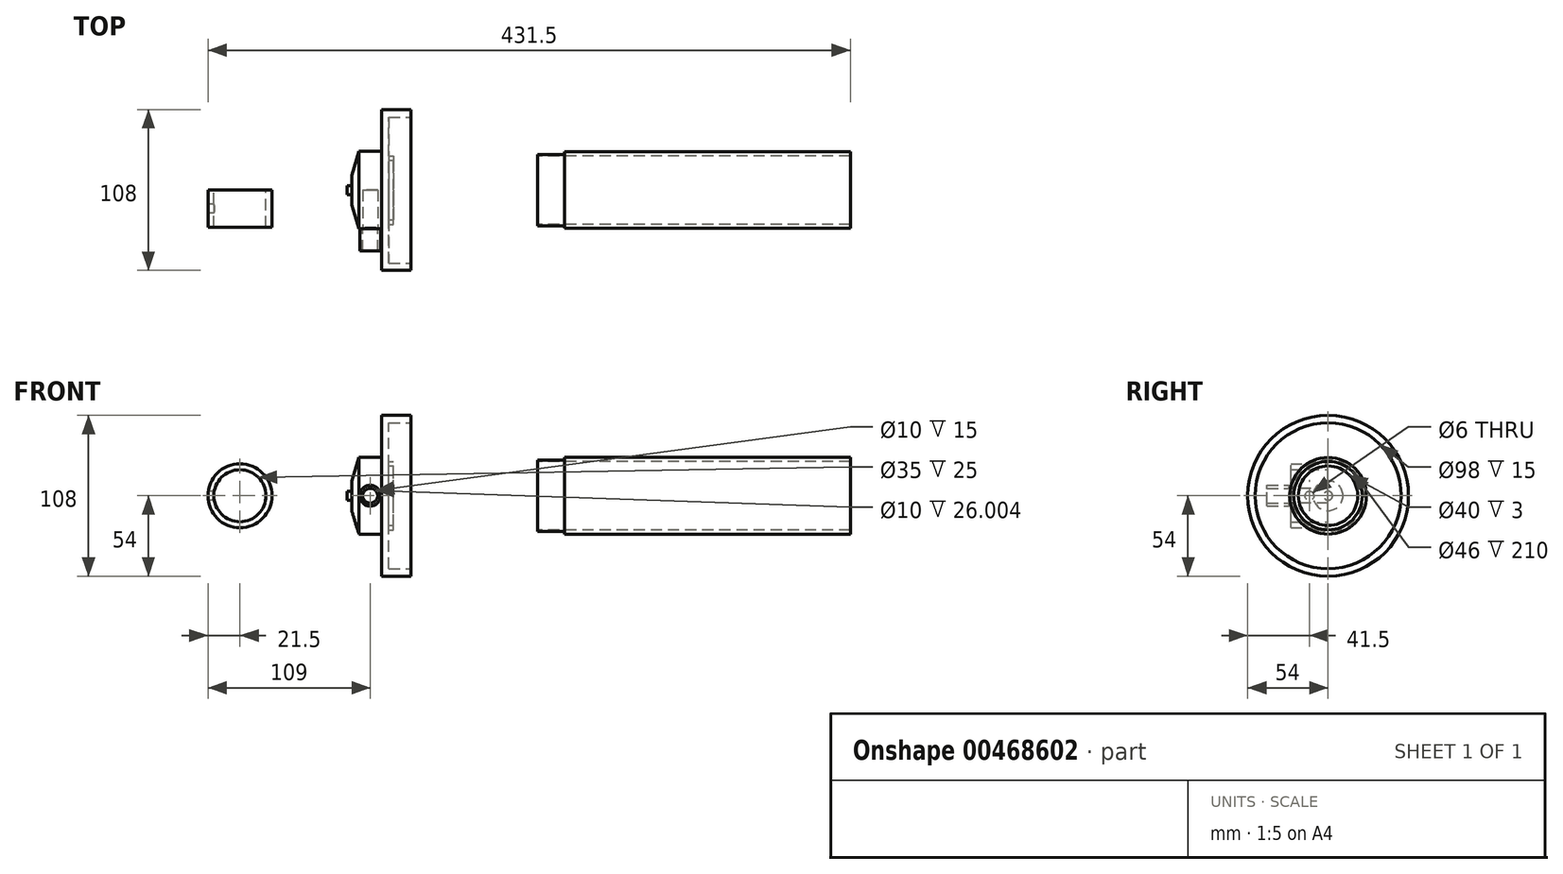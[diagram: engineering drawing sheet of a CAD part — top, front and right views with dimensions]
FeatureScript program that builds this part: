
annotation { "Feature Type Name" : "Feature", "Feature Type Description" : "" }
export const myFeature = defineFeature(function(context is Context, id is Id, definition is map)
    precondition{}
    {
        {
            var Q0;
            Q0=qCreatedBy(makeId("Front.planeOp"),FACE);
            var sketch = newSketch(context, id + "F0", { "sketchPlane" : qUnion([Q0])});
            skLineSegment(sketch, "E0", {"start": v(0, 0) * mm, "end": v(0, 25.75) * mm});
            skLineSegment(sketch, "E1", {"start": v(0, 25.75) * mm, "end": v(210, 25.75) * mm});
            skLineSegment(sketch, "E2", {"start": v(210, 25.75) * mm, "end": v(210, 23) * mm});
            skLineSegment(sketch, "E3", {"start": v(210, 23) * mm, "end": v(0, 23) * mm});
            skLineSegment(sketch, "E4", {"start": v(0, 0) * mm, "end": v(100, 0) * mm, "construction": true});
            skSolve(sketch);
        }
        {
            var Q0;
            Q0=qSketchRegion(id+"F0",true);
            var Q1;
            Q1=sQuery(id+"F0.wireOp",EDGE,"E4");
            revolve(context, id + "F1", {"entities" : qUnion([Q0]), "axis" : qUnion([Q1]), "revolveType" : RevolveType.FULL});
        }
        {
            var Q0;
            Q0=makeQuery(id+"F1.opRevolve","SWEPT_FACE",FACE,{"disambiguationData":[OSD([sQuery(id+"F0.wireOp",EDGE,"E0")])]});
            var sketch = newSketch(context, id + "F2", { "sketchPlane" : qUnion([Q0])});
            skCircle(sketch, "E5", {"center": v(0, 0) * mm, "radius": 24 * mm});
            skCircle(sketch, "E6.0", {"center": v(0, 0) * mm, "radius": 25.75 * mm});
            skSolve(sketch);
        }
        {
            var Q0;
            Q0=qSketchRegion(id+"F2",true);
            extrude(context, id + "F3", {"entities" : qUnion([Q0]), "operationType" : NewBodyOperationType.REMOVE, "oppositeDirection" : true, "depth" : 18 * mm});
        }
        {
            var Q0;
            Q0=qCreatedBy(makeId("Front.planeOp"),FACE);
            var sketch = newSketch(context, id + "F4", { "sketchPlane" : qUnion([Q0])});
            skLineSegment(sketch, "E7", {"start": v(0, 0) * mm, "end": v(-100, 0) * mm, "construction": true});
            skLineSegment(sketch, "E8", {"start": v(-100, 0) * mm, "end": v(-100, 26) * mm});
            skLineSegment(sketch, "E9", {"start": v(-100, 26) * mm, "end": v(-120, 26) * mm});
            skPoint(sketch, "E10", {"position": v(-100, 23) * mm});
            skLineSegment(sketch, "E11", {"start": v(-100, 23) * mm, "end": v(-97, 23) * mm});
            skLineSegment(sketch, "E12", {"start": v(-97, 23) * mm, "end": v(-97, 20) * mm});
            skLineSegment(sketch, "E13", {"start": v(-97, 20) * mm, "end": v(-100, 20) * mm});
            skLineSegment(sketch, "E14", {"start": v(-100, 0) * mm, "end": v(-125, 0) * mm});
            skLineSegment(sketch, "E15", {"start": v(-125, 0) * mm, "end": v(-125, 10) * mm});
            skLineSegment(sketch, "E16", {"start": v(-125, 10) * mm, "end": v(-120, 26) * mm});
            skLineSegment(sketch, "E17", {"start": v(-125, 0) * mm, "end": v(-128, 0) * mm});
            skLineSegment(sketch, "E18", {"start": v(-128, 0) * mm, "end": v(-128, 3) * mm});
            skLineSegment(sketch, "E19", {"start": v(-128, 3) * mm, "end": v(-125, 3) * mm});
            skPoint(sketch, "E20", {"position": v(-100, 49) * mm});
            skLineSegment(sketch, "E21", {"start": v(-100, 49) * mm, "end": v(-100, 26) * mm});
            skLineSegment(sketch, "E22", {"start": v(-100, 49) * mm, "end": v(-85, 49) * mm});
            skLineSegment(sketch, "E23", {"start": v(-85, 49) * mm, "end": v(-85, 54) * mm});
            skLineSegment(sketch, "E24", {"start": v(-85, 54) * mm, "end": v(-105, 54) * mm});
            skLineSegment(sketch, "E25", {"start": v(-105, 54) * mm, "end": v(-105, 26) * mm});
            skSolve(sketch);
        }
        {
            var Q0;
            Q0=qSketchRegion(id+"F4",true);
            var Q1;
            Q1=sQuery(id+"F4.wireOp",EDGE,"E14");
            revolve(context, id + "F5", {"entities" : qUnion([Q0]), "axis" : qUnion([Q1]), "revolveType" : RevolveType.FULL});
        }
        {
            var Q0;
            Q0=qCreatedBy(makeId("Front.planeOp"),FACE);
            cPlane(context, id + "F6", {"entities" : qUnion([Q0]), "cplaneType" : CPlaneType.OFFSET, "offset" : 26 * mm, "width" : 150 * mm, "height" : 150 * mm});
        }
        {
            var Q0;
            Q0=qCreatedBy(id+"F6.planeOp",FACE);
            var sketch = newSketch(context, id + "F7", { "sketchPlane" : qUnion([Q0])});
            skLineSegment(sketch, "E26.0", {"start": v(-105, 26) * mm, "end": v(-105, -26) * mm});
            skPoint(sketch, "E27", {"position": v(-105, 0) * mm});
            skPoint(sketch, "E28", {"position": v(-112.5, 0) * mm});
            skCircle(sketch, "E29", {"center": v(-112.5, 0) * mm, "radius": 7 * mm});
            skCircle(sketch, "E30", {"center": v(-112.5, 0) * mm, "radius": 5 * mm});
            skSolve(sketch);
        }
        {
            var Q0;
            Q0=qSketchRegion(id+"F7",true);
            extrude(context, id + "F8", {"entities" : qUnion([Q0]), "operationType" : NewBodyOperationType.ADD, "depth" : 15 * mm});
        }
        {
            var Q0;
            Q0=qCreatedBy(id+"F6.planeOp",FACE);
            var sketch = newSketch(context, id + "F9", { "sketchPlane" : qUnion([Q0])});
            skCircle(sketch, "E31.0", {"center": v(-112.5, 0) * mm, "radius": 7 * mm});
            skCircle(sketch, "E32.0", {"center": v(-112.5, 0) * mm, "radius": 5 * mm});
            skSolve(sketch);
        }
        {
            var Q0;
            Q0=makeQuery(id+"F9.imprint","IMPRINT",FACE,{"disambiguationData":[TD([[makeQuery(id+"F9.imprint","IMPRINT",EDGE,{"derivedFrom":sQuery(id+"F9.wireOp",EDGE,"E32.0")}),1.0]])]});
            extrude(context, id + "F10", {"entities" : qUnion([Q0]), "operationType" : NewBodyOperationType.REMOVE, "oppositeDirection" : true, "depth" : 26 * mm});
        }
        {
            var Q0;
            Q0=qCreatedBy(makeId("Front.planeOp"),FACE);
            var sketch = newSketch(context, id + "F11", { "sketchPlane" : qUnion([Q0])});
            skLineSegment(sketch, "E33", {"start": v(0, 0) * mm, "end": v(-200, 0) * mm, "construction": true});
            skCircle(sketch, "E34", {"center": v(-200, 0) * mm, "radius": 17.5 * mm});
            skCircle(sketch, "E35", {"center": v(-200, 0) * mm, "radius": 21.5 * mm});
            skSolve(sketch);
        }
        {
            var Q0;
            Q0=qSketchRegion(id+"F11",true);
            extrude(context, id + "F12", {"entities" : qUnion([Q0]), "depth" : 25 * mm});
        }
        {
            var Q0;
            Q0=qCreatedBy(makeId("Right.planeOp"),FACE);
            cPlane(context, id + "F13", {"entities" : qUnion([Q0]), "cplaneType" : CPlaneType.OFFSET, "offset" : 221.5 * mm, "oppositeDirection" : true, "width" : 150 * mm, "height" : 150 * mm});
        }
        {
            var Q0;
            Q0=qCreatedBy(id+"F13.planeOp",FACE);
            var sketch = newSketch(context, id + "F14", { "sketchPlane" : qUnion([Q0])});
            skPoint(sketch, "E36", {"position": v(-12.5, 0) * mm});
            skCircle(sketch, "E37", {"center": v(-12.5, 0) * mm, "radius": 3 * mm});
            skSolve(sketch);
        }
        {
            var Q0;
            Q0=qSketchRegion(id+"F14",true);
            extrude(context, id + "F15", {"entities" : qUnion([Q0]), "operationType" : NewBodyOperationType.REMOVE, "depth" : 6 * mm});
        }
    });
